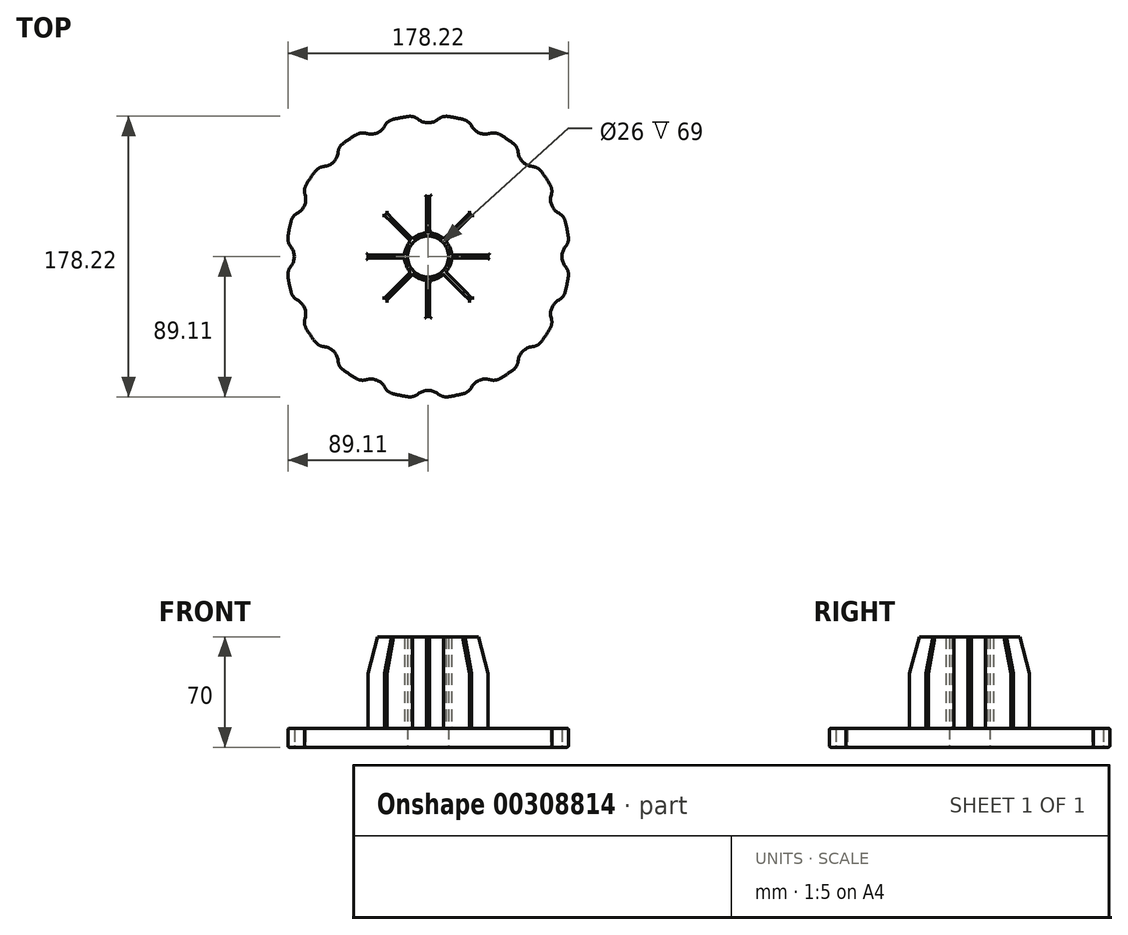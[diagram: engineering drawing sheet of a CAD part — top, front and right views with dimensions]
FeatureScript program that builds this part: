
annotation { "Feature Type Name" : "Feature", "Feature Type Description" : "" }
export const myFeature = defineFeature(function(context is Context, id is Id, definition is map)
    precondition{}
    {
        {
            var Q0;
            Q0=qCreatedBy(makeId("Top.planeOp"),FACE);
            var sketch = newSketch(context, id + "F0", { "sketchPlane" : qUnion([Q0])});
            skCircle(sketch, "E0", {"center": v(0, 0) * mm, "radius": 89.92 * mm});
            skCircle(sketch, "E1", {"center": v(-95, 0) * mm, "radius": 10 * mm});
            skCircle(sketch, "E2.1.0", {"center": v(-87.77, -36.35) * mm, "radius": 10 * mm});
            skCircle(sketch, "E2.2.0", {"center": v(-67.18, -67.18) * mm, "radius": 10 * mm});
            skCircle(sketch, "E2.3.0", {"center": v(-36.35, -87.77) * mm, "radius": 10 * mm});
            skCircle(sketch, "E2.4.0", {"center": v(0, -95) * mm, "radius": 10 * mm});
            skCircle(sketch, "E2.5.0", {"center": v(36.35, -87.77) * mm, "radius": 10 * mm});
            skCircle(sketch, "E2.6.0", {"center": v(67.18, -67.18) * mm, "radius": 10 * mm});
            skCircle(sketch, "E2.7.0", {"center": v(87.77, -36.35) * mm, "radius": 10 * mm});
            skCircle(sketch, "E2.8.0", {"center": v(95, 0) * mm, "radius": 10 * mm});
            skCircle(sketch, "E2.9.0", {"center": v(87.77, 36.35) * mm, "radius": 10 * mm});
            skCircle(sketch, "E2.10.0", {"center": v(67.18, 67.18) * mm, "radius": 10 * mm});
            skCircle(sketch, "E2.11.0", {"center": v(36.35, 87.77) * mm, "radius": 10 * mm});
            skCircle(sketch, "E2.12.0", {"center": v(0, 95) * mm, "radius": 10 * mm});
            skCircle(sketch, "E2.13.0", {"center": v(-36.35, 87.77) * mm, "radius": 10 * mm});
            skCircle(sketch, "E2.14.0", {"center": v(-67.18, 67.18) * mm, "radius": 10 * mm});
            skCircle(sketch, "E2.15.0", {"center": v(-87.77, 36.35) * mm, "radius": 10 * mm});
            skCircle(sketch, "E3", {"center": v(0, 0) * mm, "radius": 13 * mm});
            skCircle(sketch, "E4", {"center": v(0, 0) * mm, "radius": 15 * mm});
            skSolve(sketch);
        }
        {
            var Q0;
            {var subQ1=sQuery(id+"F0.wireOp",EDGE,"E0");var subQ28=sQuery(id+"F0.wireOp",EDGE,"E2.9.0");var subQ29=makeQuery(id+"F0.imprint","INTERSECT",VERTEX,{"disambiguationData":[OD(0.0)],"derivedFrom":[subQ1,subQ28]});Q0=makeQuery(id+"F0.imprint","IMPRINT",FACE,{"disambiguationData":[TD([[makeQuery(id+"F0.imprint","IMPRINT",EDGE,{"disambiguationData":[TD([[subQ29,1.0]])],"derivedFrom":subQ1}),1.0]])]});}
            extrude(context, id + "F1", {"entities" : qUnion([Q0]), "depth" : 12 * mm});
        }
        {
            var Q0;
            Q0=makeQuery(id+"F0.imprint","IMPRINT",FACE,{"disambiguationData":[TD([[makeQuery(id+"F0.imprint","IMPRINT",EDGE,{"derivedFrom":sQuery(id+"F0.wireOp",EDGE,"E3")}),-1.0]])]});
            extrude(context, id + "F2", {"entities" : qUnion([Q0]), "operationType" : NewBodyOperationType.ADD, "depth" : 70 * mm});
        }
        {
            var Q0;
            {var subQ0=sQuery(id+"F0.wireOp",EDGE,"E2.4.0");var subQ1=sQuery(id+"F0.wireOp",EDGE,"E0");Q0=makeQuery(id+"F1.opExtrude","SWEPT_EDGE",EDGE,{"disambiguationData":[OSD([subQ1,subQ0]),TDD([makeQuery(id+"F0.imprint","INTERSECT",VERTEX,{"disambiguationData":[OD(0.0)],"derivedFrom":[subQ1,subQ0]})])]});}
            var Q1;
            {var subQ0=sQuery(id+"F0.wireOp",EDGE,"E2.4.0");var subQ1=sQuery(id+"F0.wireOp",EDGE,"E0");Q1=makeQuery(id+"F1.opExtrude","SWEPT_EDGE",EDGE,{"disambiguationData":[OSD([subQ1,subQ0]),TDD([makeQuery(id+"F0.imprint","INTERSECT",VERTEX,{"disambiguationData":[OD(1.0)],"derivedFrom":[subQ1,subQ0]})])]});}
            var Q2;
            {var subQ0=sQuery(id+"F0.wireOp",EDGE,"E2.5.0");var subQ1=sQuery(id+"F0.wireOp",EDGE,"E0");Q2=makeQuery(id+"F1.opExtrude","SWEPT_EDGE",EDGE,{"disambiguationData":[OSD([subQ1,subQ0]),TDD([makeQuery(id+"F0.imprint","INTERSECT",VERTEX,{"disambiguationData":[OD(0.0)],"derivedFrom":[subQ1,subQ0]})])]});}
            var Q3;
            {var subQ0=sQuery(id+"F0.wireOp",EDGE,"E2.5.0");var subQ1=sQuery(id+"F0.wireOp",EDGE,"E0");Q3=makeQuery(id+"F1.opExtrude","SWEPT_EDGE",EDGE,{"disambiguationData":[OSD([subQ1,subQ0]),TDD([makeQuery(id+"F0.imprint","INTERSECT",VERTEX,{"disambiguationData":[OD(1.0)],"derivedFrom":[subQ1,subQ0]})])]});}
            var Q4;
            {var subQ0=sQuery(id+"F0.wireOp",EDGE,"E2.6.0");var subQ1=sQuery(id+"F0.wireOp",EDGE,"E0");Q4=makeQuery(id+"F1.opExtrude","SWEPT_EDGE",EDGE,{"disambiguationData":[OSD([subQ1,subQ0]),TDD([makeQuery(id+"F0.imprint","INTERSECT",VERTEX,{"disambiguationData":[OD(0.0)],"derivedFrom":[subQ1,subQ0]})])]});}
            var Q5;
            {var subQ0=sQuery(id+"F0.wireOp",EDGE,"E2.6.0");var subQ1=sQuery(id+"F0.wireOp",EDGE,"E0");Q5=makeQuery(id+"F1.opExtrude","SWEPT_EDGE",EDGE,{"disambiguationData":[OSD([subQ1,subQ0]),TDD([makeQuery(id+"F0.imprint","INTERSECT",VERTEX,{"disambiguationData":[OD(1.0)],"derivedFrom":[subQ1,subQ0]})])]});}
            var Q6;
            {var subQ0=sQuery(id+"F0.wireOp",EDGE,"E2.7.0");var subQ1=sQuery(id+"F0.wireOp",EDGE,"E0");Q6=makeQuery(id+"F1.opExtrude","SWEPT_EDGE",EDGE,{"disambiguationData":[OSD([subQ1,subQ0]),TDD([makeQuery(id+"F0.imprint","INTERSECT",VERTEX,{"disambiguationData":[OD(0.0)],"derivedFrom":[subQ1,subQ0]})])]});}
            var Q7;
            {var subQ0=sQuery(id+"F0.wireOp",EDGE,"E2.7.0");var subQ1=sQuery(id+"F0.wireOp",EDGE,"E0");Q7=makeQuery(id+"F1.opExtrude","SWEPT_EDGE",EDGE,{"disambiguationData":[OSD([subQ1,subQ0]),TDD([makeQuery(id+"F0.imprint","INTERSECT",VERTEX,{"disambiguationData":[OD(1.0)],"derivedFrom":[subQ1,subQ0]})])]});}
            var Q8;
            {var subQ0=sQuery(id+"F0.wireOp",EDGE,"E2.8.0");var subQ1=sQuery(id+"F0.wireOp",EDGE,"E0");Q8=makeQuery(id+"F1.opExtrude","SWEPT_EDGE",EDGE,{"disambiguationData":[OSD([subQ1,subQ0]),TDD([makeQuery(id+"F0.imprint","INTERSECT",VERTEX,{"disambiguationData":[OD(1.0)],"derivedFrom":[subQ1,subQ0]})])]});}
            var Q9;
            {var subQ0=sQuery(id+"F0.wireOp",EDGE,"E2.8.0");var subQ1=sQuery(id+"F0.wireOp",EDGE,"E0");Q9=makeQuery(id+"F1.opExtrude","SWEPT_EDGE",EDGE,{"disambiguationData":[OSD([subQ1,subQ0]),TDD([makeQuery(id+"F0.imprint","INTERSECT",VERTEX,{"disambiguationData":[OD(0.0)],"derivedFrom":[subQ1,subQ0]})])]});}
            var Q10;
            {var subQ0=sQuery(id+"F0.wireOp",EDGE,"E2.9.0");var subQ1=sQuery(id+"F0.wireOp",EDGE,"E0");Q10=makeQuery(id+"F1.opExtrude","SWEPT_EDGE",EDGE,{"disambiguationData":[OSD([subQ1,subQ0]),TDD([makeQuery(id+"F0.imprint","INTERSECT",VERTEX,{"disambiguationData":[OD(0.0)],"derivedFrom":[subQ1,subQ0]})])]});}
            var Q11;
            {var subQ0=sQuery(id+"F0.wireOp",EDGE,"E2.9.0");var subQ1=sQuery(id+"F0.wireOp",EDGE,"E0");Q11=makeQuery(id+"F1.opExtrude","SWEPT_EDGE",EDGE,{"disambiguationData":[OSD([subQ1,subQ0]),TDD([makeQuery(id+"F0.imprint","INTERSECT",VERTEX,{"disambiguationData":[OD(1.0)],"derivedFrom":[subQ1,subQ0]})])]});}
            var Q12;
            {var subQ0=sQuery(id+"F0.wireOp",EDGE,"E2.10.0");var subQ1=sQuery(id+"F0.wireOp",EDGE,"E0");Q12=makeQuery(id+"F1.opExtrude","SWEPT_EDGE",EDGE,{"disambiguationData":[OSD([subQ1,subQ0]),TDD([makeQuery(id+"F0.imprint","INTERSECT",VERTEX,{"disambiguationData":[OD(0.0)],"derivedFrom":[subQ1,subQ0]})])]});}
            var Q13;
            {var subQ0=sQuery(id+"F0.wireOp",EDGE,"E2.10.0");var subQ1=sQuery(id+"F0.wireOp",EDGE,"E0");Q13=makeQuery(id+"F1.opExtrude","SWEPT_EDGE",EDGE,{"disambiguationData":[OSD([subQ1,subQ0]),TDD([makeQuery(id+"F0.imprint","INTERSECT",VERTEX,{"disambiguationData":[OD(1.0)],"derivedFrom":[subQ1,subQ0]})])]});}
            var Q14;
            {var subQ0=sQuery(id+"F0.wireOp",EDGE,"E2.11.0");var subQ1=sQuery(id+"F0.wireOp",EDGE,"E0");Q14=makeQuery(id+"F1.opExtrude","SWEPT_EDGE",EDGE,{"disambiguationData":[OSD([subQ1,subQ0]),TDD([makeQuery(id+"F0.imprint","INTERSECT",VERTEX,{"disambiguationData":[OD(0.0)],"derivedFrom":[subQ1,subQ0]})])]});}
            var Q15;
            {var subQ0=sQuery(id+"F0.wireOp",EDGE,"E2.11.0");var subQ1=sQuery(id+"F0.wireOp",EDGE,"E0");Q15=makeQuery(id+"F1.opExtrude","SWEPT_EDGE",EDGE,{"disambiguationData":[OSD([subQ1,subQ0]),TDD([makeQuery(id+"F0.imprint","INTERSECT",VERTEX,{"disambiguationData":[OD(1.0)],"derivedFrom":[subQ1,subQ0]})])]});}
            var Q16;
            {var subQ0=sQuery(id+"F0.wireOp",EDGE,"E2.12.0");var subQ1=sQuery(id+"F0.wireOp",EDGE,"E0");Q16=makeQuery(id+"F1.opExtrude","SWEPT_EDGE",EDGE,{"disambiguationData":[OSD([subQ1,subQ0]),TDD([makeQuery(id+"F0.imprint","INTERSECT",VERTEX,{"disambiguationData":[OD(0.0)],"derivedFrom":[subQ1,subQ0]})])]});}
            var Q17;
            {var subQ0=sQuery(id+"F0.wireOp",EDGE,"E2.12.0");var subQ1=sQuery(id+"F0.wireOp",EDGE,"E0");Q17=makeQuery(id+"F1.opExtrude","SWEPT_EDGE",EDGE,{"disambiguationData":[OSD([subQ1,subQ0]),TDD([makeQuery(id+"F0.imprint","INTERSECT",VERTEX,{"disambiguationData":[OD(1.0)],"derivedFrom":[subQ1,subQ0]})])]});}
            var Q18;
            {var subQ0=sQuery(id+"F0.wireOp",EDGE,"E2.13.0");var subQ1=sQuery(id+"F0.wireOp",EDGE,"E0");Q18=makeQuery(id+"F1.opExtrude","SWEPT_EDGE",EDGE,{"disambiguationData":[OSD([subQ1,subQ0]),TDD([makeQuery(id+"F0.imprint","INTERSECT",VERTEX,{"disambiguationData":[OD(0.0)],"derivedFrom":[subQ1,subQ0]})])]});}
            var Q19;
            {var subQ0=sQuery(id+"F0.wireOp",EDGE,"E2.13.0");var subQ1=sQuery(id+"F0.wireOp",EDGE,"E0");Q19=makeQuery(id+"F1.opExtrude","SWEPT_EDGE",EDGE,{"disambiguationData":[OSD([subQ1,subQ0]),TDD([makeQuery(id+"F0.imprint","INTERSECT",VERTEX,{"disambiguationData":[OD(1.0)],"derivedFrom":[subQ1,subQ0]})])]});}
            var Q20;
            {var subQ0=sQuery(id+"F0.wireOp",EDGE,"E2.14.0");var subQ1=sQuery(id+"F0.wireOp",EDGE,"E0");Q20=makeQuery(id+"F1.opExtrude","SWEPT_EDGE",EDGE,{"disambiguationData":[OSD([subQ1,subQ0]),TDD([makeQuery(id+"F0.imprint","INTERSECT",VERTEX,{"disambiguationData":[OD(0.0)],"derivedFrom":[subQ1,subQ0]})])]});}
            var Q21;
            {var subQ0=sQuery(id+"F0.wireOp",EDGE,"E2.14.0");var subQ1=sQuery(id+"F0.wireOp",EDGE,"E0");Q21=makeQuery(id+"F1.opExtrude","SWEPT_EDGE",EDGE,{"disambiguationData":[OSD([subQ1,subQ0]),TDD([makeQuery(id+"F0.imprint","INTERSECT",VERTEX,{"disambiguationData":[OD(1.0)],"derivedFrom":[subQ1,subQ0]})])]});}
            var Q22;
            {var subQ0=sQuery(id+"F0.wireOp",EDGE,"E2.15.0");var subQ1=sQuery(id+"F0.wireOp",EDGE,"E0");Q22=makeQuery(id+"F1.opExtrude","SWEPT_EDGE",EDGE,{"disambiguationData":[OSD([subQ1,subQ0]),TDD([makeQuery(id+"F0.imprint","INTERSECT",VERTEX,{"disambiguationData":[OD(0.0)],"derivedFrom":[subQ1,subQ0]})])]});}
            var Q23;
            {var subQ0=sQuery(id+"F0.wireOp",EDGE,"E2.15.0");var subQ1=sQuery(id+"F0.wireOp",EDGE,"E0");Q23=makeQuery(id+"F1.opExtrude","SWEPT_EDGE",EDGE,{"disambiguationData":[OSD([subQ1,subQ0]),TDD([makeQuery(id+"F0.imprint","INTERSECT",VERTEX,{"disambiguationData":[OD(1.0)],"derivedFrom":[subQ1,subQ0]})])]});}
            var Q24;
            {var subQ0=sQuery(id+"F0.wireOp",EDGE,"E1");var subQ1=sQuery(id+"F0.wireOp",EDGE,"E0");Q24=makeQuery(id+"F1.opExtrude","SWEPT_EDGE",EDGE,{"disambiguationData":[OSD([subQ1,subQ0]),TDD([makeQuery(id+"F0.imprint","INTERSECT",VERTEX,{"disambiguationData":[OD(0.0)],"derivedFrom":[subQ1,subQ0]})])]});}
            var Q25;
            {var subQ0=sQuery(id+"F0.wireOp",EDGE,"E1");var subQ1=sQuery(id+"F0.wireOp",EDGE,"E0");Q25=makeQuery(id+"F1.opExtrude","SWEPT_EDGE",EDGE,{"disambiguationData":[OSD([subQ1,subQ0]),TDD([makeQuery(id+"F0.imprint","INTERSECT",VERTEX,{"disambiguationData":[OD(1.0)],"derivedFrom":[subQ1,subQ0]})])]});}
            var Q26;
            {var subQ0=sQuery(id+"F0.wireOp",EDGE,"E2.1.0");var subQ1=sQuery(id+"F0.wireOp",EDGE,"E0");Q26=makeQuery(id+"F1.opExtrude","SWEPT_EDGE",EDGE,{"disambiguationData":[OSD([subQ1,subQ0]),TDD([makeQuery(id+"F0.imprint","INTERSECT",VERTEX,{"disambiguationData":[OD(0.0)],"derivedFrom":[subQ1,subQ0]})])]});}
            var Q27;
            {var subQ0=sQuery(id+"F0.wireOp",EDGE,"E2.1.0");var subQ1=sQuery(id+"F0.wireOp",EDGE,"E0");Q27=makeQuery(id+"F1.opExtrude","SWEPT_EDGE",EDGE,{"disambiguationData":[OSD([subQ1,subQ0]),TDD([makeQuery(id+"F0.imprint","INTERSECT",VERTEX,{"disambiguationData":[OD(1.0)],"derivedFrom":[subQ1,subQ0]})])]});}
            var Q28;
            {var subQ0=sQuery(id+"F0.wireOp",EDGE,"E2.2.0");var subQ1=sQuery(id+"F0.wireOp",EDGE,"E0");Q28=makeQuery(id+"F1.opExtrude","SWEPT_EDGE",EDGE,{"disambiguationData":[OSD([subQ1,subQ0]),TDD([makeQuery(id+"F0.imprint","INTERSECT",VERTEX,{"disambiguationData":[OD(0.0)],"derivedFrom":[subQ1,subQ0]})])]});}
            var Q29;
            {var subQ0=sQuery(id+"F0.wireOp",EDGE,"E2.2.0");var subQ1=sQuery(id+"F0.wireOp",EDGE,"E0");Q29=makeQuery(id+"F1.opExtrude","SWEPT_EDGE",EDGE,{"disambiguationData":[OSD([subQ1,subQ0]),TDD([makeQuery(id+"F0.imprint","INTERSECT",VERTEX,{"disambiguationData":[OD(1.0)],"derivedFrom":[subQ1,subQ0]})])]});}
            var Q30;
            {var subQ0=sQuery(id+"F0.wireOp",EDGE,"E2.3.0");var subQ1=sQuery(id+"F0.wireOp",EDGE,"E0");Q30=makeQuery(id+"F1.opExtrude","SWEPT_EDGE",EDGE,{"disambiguationData":[OSD([subQ1,subQ0]),TDD([makeQuery(id+"F0.imprint","INTERSECT",VERTEX,{"disambiguationData":[OD(0.0)],"derivedFrom":[subQ1,subQ0]})])]});}
            var Q31;
            {var subQ0=sQuery(id+"F0.wireOp",EDGE,"E2.3.0");var subQ1=sQuery(id+"F0.wireOp",EDGE,"E0");Q31=makeQuery(id+"F1.opExtrude","SWEPT_EDGE",EDGE,{"disambiguationData":[OSD([subQ1,subQ0]),TDD([makeQuery(id+"F0.imprint","INTERSECT",VERTEX,{"disambiguationData":[OD(1.0)],"derivedFrom":[subQ1,subQ0]})])]});}
            fillet(context, id + "F3", {"entities" : qUnion([Q0, Q1, Q2, Q3, Q4, Q5, Q6, Q7, Q8, Q9, Q10, Q11, Q12, Q13, Q14, Q15, Q16, Q17, Q18, Q19, Q20, Q21, Q22, Q23, Q24, Q25, Q26, Q27, Q28, Q29, Q30, Q31]), "radius" : 8 * mm, "tangentPropagation" : true, "allowEdgeOverflow" : false});
        }
        {
            var Q0;
            Q0=qCreatedBy(makeId("Front.planeOp"),FACE);
            var sketch = newSketch(context, id + "F4", { "sketchPlane" : qUnion([Q0])});
            skLineSegment(sketch, "E5", {"start": v(14.5, 70) * mm, "end": v(32, 70) * mm});
            skLineSegment(sketch, "E6", {"start": v(32, 70) * mm, "end": v(38.1, 47) * mm});
            skLineSegment(sketch, "E7", {"start": v(38.1, 47) * mm, "end": v(38.1, 8) * mm});
            skLineSegment(sketch, "E8", {"start": v(38.1, 8) * mm, "end": v(14.5, 8) * mm});
            skLineSegment(sketch, "E9", {"start": v(14.5, 8) * mm, "end": v(14.5, 70) * mm});
            skSolve(sketch);
        }
        {
            var Q0;
            Q0=makeQuery(id+"F4.imprint","IMPRINT",FACE,{"disambiguationData":[TD([[makeQuery(id+"F4.imprint","IMPRINT",EDGE,{"derivedFrom":sQuery(id+"F4.wireOp",EDGE,"E5")}),-1.0]])]});
            extrude(context, id + "F5", {"entities" : qUnion([Q0]), "endBound" : BoundingType.SYMMETRIC, "depth" : 2 * mm});
        }
        {
            var Q0;
            Q0=makeQuery(id+"F5.opExtrude","SWEPT_BODY",BODY,{"disambiguationData":[OSD([sQuery(id+"F4.wireOp",EDGE,"E5"),sQuery(id+"F4.wireOp",EDGE,"E6"),sQuery(id+"F4.wireOp",EDGE,"E7"),sQuery(id+"F4.wireOp",EDGE,"E8"),sQuery(id+"F4.wireOp",EDGE,"E9")])]});
            var Q1;
            Q1=makeQuery(id+"F2.opExtrude","SWEPT_FACE",FACE,{"disambiguationData":[OSD([sQuery(id+"F0.wireOp",EDGE,"E4")])]});
            circularPattern(context, id + "F6", {"operationType" : NewBodyOperationType.ADD, "entities" : qUnion([Q0]), "axis" : qUnion([Q1]), "angle" : 360 * degree, "instanceCount" : 8, "equalSpace" : true});
        }
        {
            var Q0;
            Q0=makeQuery(id+"F1.opExtrude","CAP_FACE",FACE,{"disambiguationData":[OSD([sQuery(id+"F0.wireOp",EDGE,"E0"),sQuery(id+"F0.wireOp",EDGE,"E1"),sQuery(id+"F0.wireOp",EDGE,"E2.1.0"),sQuery(id+"F0.wireOp",EDGE,"E2.2.0"),sQuery(id+"F0.wireOp",EDGE,"E2.3.0"),sQuery(id+"F0.wireOp",EDGE,"E2.4.0"),sQuery(id+"F0.wireOp",EDGE,"E2.5.0"),sQuery(id+"F0.wireOp",EDGE,"E2.6.0"),sQuery(id+"F0.wireOp",EDGE,"E2.7.0"),sQuery(id+"F0.wireOp",EDGE,"E2.8.0"),sQuery(id+"F0.wireOp",EDGE,"E2.9.0"),sQuery(id+"F0.wireOp",EDGE,"E2.10.0"),sQuery(id+"F0.wireOp",EDGE,"E2.11.0"),sQuery(id+"F0.wireOp",EDGE,"E2.12.0"),sQuery(id+"F0.wireOp",EDGE,"E2.13.0"),sQuery(id+"F0.wireOp",EDGE,"E2.14.0"),sQuery(id+"F0.wireOp",EDGE,"E2.15.0"),sQuery(id+"F0.wireOp",EDGE,"E4")])],"isStart":false});
            var Q1;
            {var subQ0=sQuery(id+"F0.wireOp",EDGE,"E4");Q1=makeQuery(id+"F2.boolean.opBoolean","MERGE",FACE,{"derivedFrom":[makeQuery(id+"F1.opExtrude","CAP_FACE",FACE,{"disambiguationData":[OSD([sQuery(id+"F0.wireOp",EDGE,"E0"),sQuery(id+"F0.wireOp",EDGE,"E1"),sQuery(id+"F0.wireOp",EDGE,"E2.1.0"),sQuery(id+"F0.wireOp",EDGE,"E2.2.0"),sQuery(id+"F0.wireOp",EDGE,"E2.3.0"),sQuery(id+"F0.wireOp",EDGE,"E2.4.0"),sQuery(id+"F0.wireOp",EDGE,"E2.5.0"),sQuery(id+"F0.wireOp",EDGE,"E2.6.0"),sQuery(id+"F0.wireOp",EDGE,"E2.7.0"),sQuery(id+"F0.wireOp",EDGE,"E2.8.0"),sQuery(id+"F0.wireOp",EDGE,"E2.9.0"),sQuery(id+"F0.wireOp",EDGE,"E2.10.0"),sQuery(id+"F0.wireOp",EDGE,"E2.11.0"),sQuery(id+"F0.wireOp",EDGE,"E2.12.0"),sQuery(id+"F0.wireOp",EDGE,"E2.13.0"),sQuery(id+"F0.wireOp",EDGE,"E2.14.0"),sQuery(id+"F0.wireOp",EDGE,"E2.15.0"),subQ0])],"isStart":true}),makeQuery(id+"F2.opExtrude","CAP_FACE",FACE,{"disambiguationData":[OSD([sQuery(id+"F0.wireOp",EDGE,"E3"),subQ0])],"isStart":true})]});}
            fillet(context, id + "F7", {"entities" : qUnion([Q0, Q1]), "radius" : 1 * mm, "tangentPropagation" : true, "allowEdgeOverflow" : false});
        }
    });
